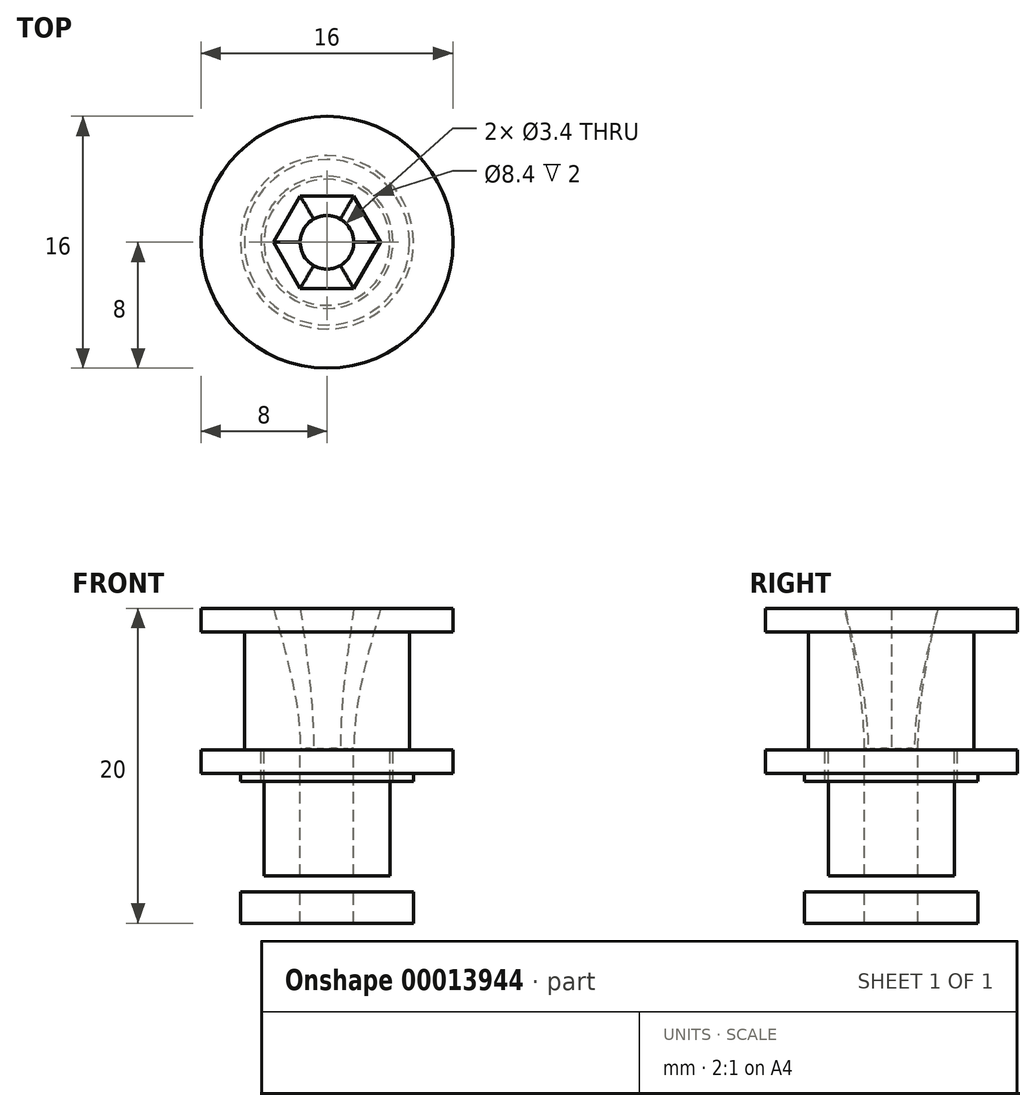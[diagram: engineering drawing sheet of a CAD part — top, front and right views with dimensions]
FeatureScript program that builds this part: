
annotation { "Feature Type Name" : "Feature", "Feature Type Description" : "" }
export const myFeature = defineFeature(function(context is Context, id is Id, definition is map)
    precondition{}
    {
        {
            var Q0;
            Q0=qCreatedBy(makeId("Top.planeOp"),FACE);
            var sketch = newSketch(context, id + "F0", { "sketchPlane" : qUnion([Q0])});
            skLineSegment(sketch, "E0", {"start": v(-19.17, 17.78) * mm, "end": v(-18.17, 17.78) * mm});
            skLineSegment(sketch, "E1", {"start": v(-18.17, 17.78) * mm, "end": v(-18.17, 18.4) * mm});
            skArc(sketch, "E2", {"start": v(-18.67, 18.85) * mm, "mid": v(-18.88, 19.07) * mm, "end": v(-19.17, 19.16) * mm});
            skArc(sketch, "E3", {"start": v(-18.58, 18.54) * mm, "mid": v(-18.61, 18.7) * mm, "end": v(-18.67, 18.85) * mm});
            skArc(sketch, "E4", {"start": v(-18.58, 18.54) * mm, "mid": v(-18.53, 18.44) * mm, "end": v(-18.43, 18.4) * mm});
            skLineSegment(sketch, "E5", {"start": v(-18.43, 18.4) * mm, "end": v(-18.17, 18.4) * mm});
            skArc(sketch, "E6.0.MirrorCS", {"start": v(-19.67, 18.85) * mm, "mid": v(-19.47, 19.07) * mm, "end": v(-19.17, 19.16) * mm});
            skArc(sketch, "E7.0.MirrorCS", {"start": v(-19.76, 18.54) * mm, "mid": v(-19.73, 18.7) * mm, "end": v(-19.67, 18.85) * mm});
            skArc(sketch, "E8.0.MirrorCS", {"start": v(-19.76, 18.54) * mm, "mid": v(-19.81, 18.44) * mm, "end": v(-19.91, 18.4) * mm});
            skLineSegment(sketch, "E9.0.MirrorCS", {"start": v(-19.91, 18.4) * mm, "end": v(-20.17, 18.4) * mm});
            skLineSegment(sketch, "E10.0.MirrorCS", {"start": v(-20.17, 17.78) * mm, "end": v(-20.17, 18.4) * mm});
            skLineSegment(sketch, "E11.0.MirrorCS", {"start": v(-19.17, 17.78) * mm, "end": v(-20.17, 17.78) * mm});
            skLineSegment(sketch, "E12.direction1", {"start": v(-20.17, 17.78) * mm, "end": v(-18.17, 17.78) * mm, "construction": true});
            skLineSegment(sketch, "E13", {"start": v(-20.17, 18.15) * mm, "end": v(-18.17, 18.15) * mm, "construction": true});
            skPoint(sketch, "E14", {"position": v(0, -5.25) * mm});
            skArc(sketch, "E15", {"start": v(0.51, -5.6) * mm, "mid": v(0, -5.25) * mm, "end": v(-0.51, -5.6) * mm});
            skArc(sketch, "E16", {"start": v(-0.51, -5.6) * mm, "mid": v(-0.56, -5.71) * mm, "end": v(-0.59, -5.83) * mm});
            skArc(sketch, "E17", {"start": v(0.59, -5.83) * mm, "mid": v(0.56, -5.71) * mm, "end": v(0.51, -5.6) * mm});
            skArc(sketch, "E18", {"start": v(0.72, -5.96) * mm, "mid": v(0.94, -5.93) * mm, "end": v(1.16, -5.89) * mm});
            skArc(sketch, "E19", {"start": v(0.59, -5.83) * mm, "mid": v(0.66, -5.94) * mm, "end": v(0.8, -5.95) * mm});
            skArc(sketch, "E20", {"start": v(-0.59, -5.83) * mm, "mid": v(-0.66, -5.94) * mm, "end": v(-0.8, -5.95) * mm});
            skArc(sketch, "E21.1.0", {"start": v(2.22, -5.16) * mm, "mid": v(1.62, -5) * mm, "end": v(1.24, -5.48) * mm});
            skPoint(sketch, "E21.1.1", {"position": v(1.62, -5) * mm});
            skArc(sketch, "E21.1.2", {"start": v(1.24, -5.48) * mm, "mid": v(1.23, -5.6) * mm, "end": v(1.24, -5.73) * mm});
            skArc(sketch, "E21.1.3", {"start": v(2.36, -5.37) * mm, "mid": v(2.47, -5.44) * mm, "end": v(2.6, -5.41) * mm});
            skArc(sketch, "E21.1.4", {"start": v(1.24, -5.73) * mm, "mid": v(1.2, -5.85) * mm, "end": v(1.08, -5.9) * mm});
            skArc(sketch, "E21.1.5", {"start": v(2.36, -5.37) * mm, "mid": v(2.3, -5.26) * mm, "end": v(2.22, -5.16) * mm});
            skArc(sketch, "E22.3.2.0", {"start": v(3.7, -4.22) * mm, "mid": v(3.09, -4.25) * mm, "end": v(2.87, -4.83) * mm});
            skPoint(sketch, "E22.4.2.0", {"position": v(3.09, -4.25) * mm});
            skArc(sketch, "E22.5.2.0", {"start": v(2.87, -4.83) * mm, "mid": v(2.9, -4.95) * mm, "end": v(2.95, -5.07) * mm});
            skArc(sketch, "E22.9.2.0", {"start": v(3.9, -4.37) * mm, "mid": v(4.03, -4.41) * mm, "end": v(4.14, -4.35) * mm});
            skArc(sketch, "E22.13.2.0", {"start": v(2.95, -5.07) * mm, "mid": v(2.95, -5.2) * mm, "end": v(2.85, -5.28) * mm});
            skArc(sketch, "E22.17.2.0", {"start": v(3.9, -4.37) * mm, "mid": v(3.81, -4.3) * mm, "end": v(3.7, -4.22) * mm});
            skArc(sketch, "E22.3.3.0", {"start": v(4.83, -2.87) * mm, "mid": v(4.25, -3.09) * mm, "end": v(4.22, -3.7) * mm});
            skPoint(sketch, "E22.4.3.0", {"position": v(4.25, -3.09) * mm});
            skArc(sketch, "E22.5.3.0", {"start": v(4.22, -3.7) * mm, "mid": v(4.3, -3.81) * mm, "end": v(4.37, -3.9) * mm});
            skArc(sketch, "E22.9.3.0", {"start": v(5.07, -2.95) * mm, "mid": v(5.2, -2.95) * mm, "end": v(5.28, -2.85) * mm});
            skArc(sketch, "E22.13.3.0", {"start": v(4.37, -3.9) * mm, "mid": v(4.41, -4.03) * mm, "end": v(4.35, -4.14) * mm});
            skArc(sketch, "E22.17.3.0", {"start": v(5.07, -2.95) * mm, "mid": v(4.95, -2.9) * mm, "end": v(4.83, -2.87) * mm});
            skArc(sketch, "E22.3.4.0", {"start": v(5.48, -1.24) * mm, "mid": v(5, -1.62) * mm, "end": v(5.16, -2.22) * mm});
            skPoint(sketch, "E22.4.4.0", {"position": v(5, -1.62) * mm});
            skArc(sketch, "E22.5.4.0", {"start": v(5.16, -2.22) * mm, "mid": v(5.26, -2.3) * mm, "end": v(5.37, -2.36) * mm});
            skArc(sketch, "E22.9.4.0", {"start": v(5.73, -1.24) * mm, "mid": v(5.85, -1.2) * mm, "end": v(5.9, -1.08) * mm});
            skArc(sketch, "E22.13.4.0", {"start": v(5.37, -2.36) * mm, "mid": v(5.44, -2.47) * mm, "end": v(5.41, -2.6) * mm});
            skArc(sketch, "E22.17.4.0", {"start": v(5.73, -1.24) * mm, "mid": v(5.6, -1.23) * mm, "end": v(5.48, -1.24) * mm});
            skArc(sketch, "E22.3.5.0", {"start": v(5.6, 0.51) * mm, "mid": v(5.25, 0) * mm, "end": v(5.6, -0.51) * mm});
            skPoint(sketch, "E22.4.5.0", {"position": v(5.25, 0) * mm});
            skArc(sketch, "E22.5.5.0", {"start": v(5.6, -0.51) * mm, "mid": v(5.71, -0.56) * mm, "end": v(5.83, -0.59) * mm});
            skArc(sketch, "E22.9.5.0", {"start": v(5.83, 0.59) * mm, "mid": v(5.94, 0.66) * mm, "end": v(5.95, 0.8) * mm});
            skArc(sketch, "E22.13.5.0", {"start": v(5.83, -0.59) * mm, "mid": v(5.94, -0.66) * mm, "end": v(5.95, -0.8) * mm});
            skArc(sketch, "E22.17.5.0", {"start": v(5.83, 0.59) * mm, "mid": v(5.71, 0.56) * mm, "end": v(5.6, 0.51) * mm});
            skArc(sketch, "E22.3.6.0", {"start": v(5.16, 2.22) * mm, "mid": v(5, 1.62) * mm, "end": v(5.48, 1.24) * mm});
            skPoint(sketch, "E22.4.6.0", {"position": v(5, 1.62) * mm});
            skArc(sketch, "E22.5.6.0", {"start": v(5.48, 1.24) * mm, "mid": v(5.6, 1.23) * mm, "end": v(5.73, 1.24) * mm});
            skArc(sketch, "E22.9.6.0", {"start": v(5.37, 2.36) * mm, "mid": v(5.44, 2.47) * mm, "end": v(5.41, 2.6) * mm});
            skArc(sketch, "E22.13.6.0", {"start": v(5.73, 1.24) * mm, "mid": v(5.85, 1.2) * mm, "end": v(5.9, 1.08) * mm});
            skArc(sketch, "E22.17.6.0", {"start": v(5.37, 2.36) * mm, "mid": v(5.26, 2.3) * mm, "end": v(5.16, 2.22) * mm});
            skArc(sketch, "E22.3.7.0", {"start": v(4.22, 3.7) * mm, "mid": v(4.25, 3.09) * mm, "end": v(4.83, 2.87) * mm});
            skPoint(sketch, "E22.4.7.0", {"position": v(4.25, 3.09) * mm});
            skArc(sketch, "E22.5.7.0", {"start": v(4.83, 2.87) * mm, "mid": v(4.95, 2.9) * mm, "end": v(5.07, 2.95) * mm});
            skArc(sketch, "E22.9.7.0", {"start": v(4.37, 3.9) * mm, "mid": v(4.41, 4.03) * mm, "end": v(4.35, 4.14) * mm});
            skArc(sketch, "E22.13.7.0", {"start": v(5.07, 2.95) * mm, "mid": v(5.2, 2.95) * mm, "end": v(5.28, 2.85) * mm});
            skArc(sketch, "E22.17.7.0", {"start": v(4.37, 3.9) * mm, "mid": v(4.3, 3.81) * mm, "end": v(4.22, 3.7) * mm});
            skArc(sketch, "E22.3.8.0", {"start": v(2.87, 4.83) * mm, "mid": v(3.09, 4.25) * mm, "end": v(3.7, 4.22) * mm});
            skPoint(sketch, "E22.4.8.0", {"position": v(3.09, 4.25) * mm});
            skArc(sketch, "E22.5.8.0", {"start": v(3.7, 4.22) * mm, "mid": v(3.81, 4.3) * mm, "end": v(3.9, 4.37) * mm});
            skArc(sketch, "E22.9.8.0", {"start": v(2.95, 5.07) * mm, "mid": v(2.95, 5.2) * mm, "end": v(2.85, 5.28) * mm});
            skArc(sketch, "E22.13.8.0", {"start": v(3.9, 4.37) * mm, "mid": v(4.03, 4.41) * mm, "end": v(4.14, 4.35) * mm});
            skArc(sketch, "E22.17.8.0", {"start": v(2.95, 5.07) * mm, "mid": v(2.9, 4.95) * mm, "end": v(2.87, 4.83) * mm});
            skArc(sketch, "E22.3.9.0", {"start": v(1.24, 5.48) * mm, "mid": v(1.62, 5) * mm, "end": v(2.22, 5.16) * mm});
            skPoint(sketch, "E22.4.9.0", {"position": v(1.62, 5) * mm});
            skArc(sketch, "E22.5.9.0", {"start": v(2.22, 5.16) * mm, "mid": v(2.3, 5.26) * mm, "end": v(2.36, 5.37) * mm});
            skArc(sketch, "E22.9.9.0", {"start": v(1.24, 5.73) * mm, "mid": v(1.2, 5.85) * mm, "end": v(1.08, 5.9) * mm});
            skArc(sketch, "E22.13.9.0", {"start": v(2.36, 5.37) * mm, "mid": v(2.47, 5.44) * mm, "end": v(2.6, 5.41) * mm});
            skArc(sketch, "E22.17.9.0", {"start": v(1.24, 5.73) * mm, "mid": v(1.23, 5.6) * mm, "end": v(1.24, 5.48) * mm});
            skArc(sketch, "E22.3.10.0", {"start": v(-0.51, 5.6) * mm, "mid": v(0, 5.25) * mm, "end": v(0.51, 5.6) * mm});
            skPoint(sketch, "E22.4.10.0", {"position": v(0, 5.25) * mm});
            skArc(sketch, "E22.5.10.0", {"start": v(0.51, 5.6) * mm, "mid": v(0.56, 5.71) * mm, "end": v(0.59, 5.83) * mm});
            skArc(sketch, "E22.9.10.0", {"start": v(-0.59, 5.83) * mm, "mid": v(-0.66, 5.94) * mm, "end": v(-0.8, 5.95) * mm});
            skArc(sketch, "E22.13.10.0", {"start": v(0.59, 5.83) * mm, "mid": v(0.66, 5.94) * mm, "end": v(0.8, 5.95) * mm});
            skArc(sketch, "E22.17.10.0", {"start": v(-0.59, 5.83) * mm, "mid": v(-0.56, 5.71) * mm, "end": v(-0.51, 5.6) * mm});
            skArc(sketch, "E22.3.11.0", {"start": v(-2.22, 5.16) * mm, "mid": v(-1.62, 5) * mm, "end": v(-1.24, 5.48) * mm});
            skPoint(sketch, "E22.4.11.0", {"position": v(-1.62, 5) * mm});
            skArc(sketch, "E22.5.11.0", {"start": v(-1.24, 5.48) * mm, "mid": v(-1.23, 5.6) * mm, "end": v(-1.24, 5.73) * mm});
            skArc(sketch, "E22.9.11.0", {"start": v(-2.36, 5.37) * mm, "mid": v(-2.47, 5.44) * mm, "end": v(-2.6, 5.41) * mm});
            skArc(sketch, "E22.13.11.0", {"start": v(-1.24, 5.73) * mm, "mid": v(-1.2, 5.85) * mm, "end": v(-1.08, 5.9) * mm});
            skArc(sketch, "E22.17.11.0", {"start": v(-2.36, 5.37) * mm, "mid": v(-2.3, 5.26) * mm, "end": v(-2.22, 5.16) * mm});
            skArc(sketch, "E22.3.12.0", {"start": v(-3.7, 4.22) * mm, "mid": v(-3.09, 4.25) * mm, "end": v(-2.87, 4.83) * mm});
            skPoint(sketch, "E22.4.12.0", {"position": v(-3.09, 4.25) * mm});
            skArc(sketch, "E22.5.12.0", {"start": v(-2.87, 4.83) * mm, "mid": v(-2.9, 4.95) * mm, "end": v(-2.95, 5.07) * mm});
            skArc(sketch, "E22.9.12.0", {"start": v(-3.9, 4.37) * mm, "mid": v(-4.03, 4.41) * mm, "end": v(-4.14, 4.35) * mm});
            skArc(sketch, "E22.13.12.0", {"start": v(-2.95, 5.07) * mm, "mid": v(-2.95, 5.2) * mm, "end": v(-2.85, 5.28) * mm});
            skArc(sketch, "E22.17.12.0", {"start": v(-3.9, 4.37) * mm, "mid": v(-3.81, 4.3) * mm, "end": v(-3.7, 4.22) * mm});
            skArc(sketch, "E22.3.13.0", {"start": v(-4.83, 2.87) * mm, "mid": v(-4.25, 3.09) * mm, "end": v(-4.22, 3.7) * mm});
            skPoint(sketch, "E22.4.13.0", {"position": v(-4.25, 3.09) * mm});
            skArc(sketch, "E22.5.13.0", {"start": v(-4.22, 3.7) * mm, "mid": v(-4.3, 3.81) * mm, "end": v(-4.37, 3.9) * mm});
            skArc(sketch, "E22.9.13.0", {"start": v(-5.07, 2.95) * mm, "mid": v(-5.2, 2.95) * mm, "end": v(-5.28, 2.85) * mm});
            skArc(sketch, "E22.13.13.0", {"start": v(-4.37, 3.9) * mm, "mid": v(-4.41, 4.03) * mm, "end": v(-4.35, 4.14) * mm});
            skArc(sketch, "E22.17.13.0", {"start": v(-5.07, 2.95) * mm, "mid": v(-4.95, 2.9) * mm, "end": v(-4.83, 2.87) * mm});
            skArc(sketch, "E22.3.14.0", {"start": v(-5.48, 1.24) * mm, "mid": v(-5, 1.62) * mm, "end": v(-5.16, 2.22) * mm});
            skPoint(sketch, "E22.4.14.0", {"position": v(-5, 1.62) * mm});
            skArc(sketch, "E22.5.14.0", {"start": v(-5.16, 2.22) * mm, "mid": v(-5.26, 2.3) * mm, "end": v(-5.37, 2.36) * mm});
            skArc(sketch, "E22.9.14.0", {"start": v(-5.73, 1.24) * mm, "mid": v(-5.85, 1.2) * mm, "end": v(-5.9, 1.08) * mm});
            skArc(sketch, "E22.13.14.0", {"start": v(-5.37, 2.36) * mm, "mid": v(-5.44, 2.47) * mm, "end": v(-5.41, 2.6) * mm});
            skArc(sketch, "E22.17.14.0", {"start": v(-5.73, 1.24) * mm, "mid": v(-5.6, 1.23) * mm, "end": v(-5.48, 1.24) * mm});
            skArc(sketch, "E22.3.15.0", {"start": v(-5.6, -0.51) * mm, "mid": v(-5.25, 0) * mm, "end": v(-5.6, 0.51) * mm});
            skPoint(sketch, "E22.4.15.0", {"position": v(-5.25, 0) * mm});
            skArc(sketch, "E22.5.15.0", {"start": v(-5.6, 0.51) * mm, "mid": v(-5.71, 0.56) * mm, "end": v(-5.83, 0.59) * mm});
            skArc(sketch, "E22.9.15.0", {"start": v(-5.83, -0.59) * mm, "mid": v(-5.94, -0.66) * mm, "end": v(-5.95, -0.8) * mm});
            skArc(sketch, "E22.13.15.0", {"start": v(-5.83, 0.59) * mm, "mid": v(-5.94, 0.66) * mm, "end": v(-5.95, 0.8) * mm});
            skArc(sketch, "E22.17.15.0", {"start": v(-5.83, -0.59) * mm, "mid": v(-5.71, -0.56) * mm, "end": v(-5.6, -0.51) * mm});
            skArc(sketch, "E22.3.16.0", {"start": v(-5.16, -2.22) * mm, "mid": v(-5, -1.62) * mm, "end": v(-5.48, -1.24) * mm});
            skPoint(sketch, "E22.4.16.0", {"position": v(-5, -1.62) * mm});
            skArc(sketch, "E22.5.16.0", {"start": v(-5.48, -1.24) * mm, "mid": v(-5.6, -1.23) * mm, "end": v(-5.73, -1.24) * mm});
            skArc(sketch, "E22.9.16.0", {"start": v(-5.37, -2.36) * mm, "mid": v(-5.44, -2.47) * mm, "end": v(-5.41, -2.6) * mm});
            skArc(sketch, "E22.13.16.0", {"start": v(-5.73, -1.24) * mm, "mid": v(-5.85, -1.2) * mm, "end": v(-5.9, -1.08) * mm});
            skArc(sketch, "E22.17.16.0", {"start": v(-5.37, -2.36) * mm, "mid": v(-5.26, -2.3) * mm, "end": v(-5.16, -2.22) * mm});
            skArc(sketch, "E22.3.17.0", {"start": v(-4.22, -3.7) * mm, "mid": v(-4.25, -3.09) * mm, "end": v(-4.83, -2.87) * mm});
            skPoint(sketch, "E22.4.17.0", {"position": v(-4.25, -3.09) * mm});
            skArc(sketch, "E22.5.17.0", {"start": v(-4.83, -2.87) * mm, "mid": v(-4.95, -2.9) * mm, "end": v(-5.07, -2.95) * mm});
            skArc(sketch, "E22.9.17.0", {"start": v(-4.37, -3.9) * mm, "mid": v(-4.41, -4.03) * mm, "end": v(-4.35, -4.14) * mm});
            skArc(sketch, "E22.13.17.0", {"start": v(-5.07, -2.95) * mm, "mid": v(-5.2, -2.95) * mm, "end": v(-5.28, -2.85) * mm});
            skArc(sketch, "E22.17.17.0", {"start": v(-4.37, -3.9) * mm, "mid": v(-4.3, -3.81) * mm, "end": v(-4.22, -3.7) * mm});
            skArc(sketch, "E22.3.18.0", {"start": v(-2.87, -4.83) * mm, "mid": v(-3.09, -4.25) * mm, "end": v(-3.7, -4.22) * mm});
            skPoint(sketch, "E22.4.18.0", {"position": v(-3.09, -4.25) * mm});
            skArc(sketch, "E22.5.18.0", {"start": v(-3.7, -4.22) * mm, "mid": v(-3.81, -4.3) * mm, "end": v(-3.9, -4.37) * mm});
            skArc(sketch, "E22.9.18.0", {"start": v(-2.95, -5.07) * mm, "mid": v(-2.95, -5.2) * mm, "end": v(-2.85, -5.28) * mm});
            skArc(sketch, "E22.13.18.0", {"start": v(-3.9, -4.37) * mm, "mid": v(-4.03, -4.41) * mm, "end": v(-4.14, -4.35) * mm});
            skArc(sketch, "E22.17.18.0", {"start": v(-2.95, -5.07) * mm, "mid": v(-2.9, -4.95) * mm, "end": v(-2.87, -4.83) * mm});
            skArc(sketch, "E22.3.19.0", {"start": v(-1.24, -5.48) * mm, "mid": v(-1.62, -5) * mm, "end": v(-2.22, -5.16) * mm});
            skPoint(sketch, "E22.4.19.0", {"position": v(-1.62, -5) * mm});
            skArc(sketch, "E22.5.19.0", {"start": v(-2.22, -5.16) * mm, "mid": v(-2.3, -5.26) * mm, "end": v(-2.36, -5.37) * mm});
            skArc(sketch, "E22.9.19.0", {"start": v(-1.24, -5.73) * mm, "mid": v(-1.2, -5.85) * mm, "end": v(-1.08, -5.9) * mm});
            skArc(sketch, "E22.13.19.0", {"start": v(-2.36, -5.37) * mm, "mid": v(-2.47, -5.44) * mm, "end": v(-2.6, -5.41) * mm});
            skArc(sketch, "E22.17.19.0", {"start": v(-1.24, -5.73) * mm, "mid": v(-1.23, -5.6) * mm, "end": v(-1.24, -5.48) * mm});
            skArc(sketch, "E23.trimOffspring", {"start": v(2.52, -5.44) * mm, "mid": v(2.72, -5.35) * mm, "end": v(2.92, -5.24) * mm});
            skArc(sketch, "E24.trimOffspring", {"start": v(4.08, -4.4) * mm, "mid": v(4.24, -4.24) * mm, "end": v(4.4, -4.08) * mm});
            skArc(sketch, "E25.trimOffspring", {"start": v(5.24, -2.92) * mm, "mid": v(5.33, -2.76) * mm, "end": v(5.41, -2.6) * mm});
            skArc(sketch, "E26.trimOffspring", {"start": v(5.89, -1.16) * mm, "mid": v(5.93, -0.94) * mm, "end": v(5.96, -0.72) * mm});
            skArc(sketch, "E27.trimOffspring", {"start": v(5.44, 2.52) * mm, "mid": v(5.35, 2.72) * mm, "end": v(5.24, 2.92) * mm});
            skArc(sketch, "E28.trimOffspring", {"start": v(4.4, 4.08) * mm, "mid": v(4.24, 4.24) * mm, "end": v(4.08, 4.4) * mm});
            skArc(sketch, "E29.trimOffspring", {"start": v(5.96, 0.72) * mm, "mid": v(5.93, 0.94) * mm, "end": v(5.89, 1.16) * mm});
            skArc(sketch, "E30.trimOffspring", {"start": v(2.92, 5.24) * mm, "mid": v(2.72, 5.35) * mm, "end": v(2.52, 5.44) * mm});
            skArc(sketch, "E31.trimOffspring", {"start": v(1.16, 5.89) * mm, "mid": v(0.94, 5.93) * mm, "end": v(0.72, 5.96) * mm});
            skArc(sketch, "E32.trimOffspring", {"start": v(-0.72, 5.96) * mm, "mid": v(-0.94, 5.93) * mm, "end": v(-1.16, 5.89) * mm});
            skArc(sketch, "E33.trimOffspring", {"start": v(-2.52, 5.44) * mm, "mid": v(-2.72, 5.35) * mm, "end": v(-2.92, 5.24) * mm});
            skArc(sketch, "E34.trimOffspring", {"start": v(-4.08, 4.4) * mm, "mid": v(-4.24, 4.24) * mm, "end": v(-4.4, 4.08) * mm});
            skArc(sketch, "E35.trimOffspring", {"start": v(-5.24, 2.92) * mm, "mid": v(-5.35, 2.72) * mm, "end": v(-5.44, 2.52) * mm});
            skArc(sketch, "E36.trimOffspring", {"start": v(-5.89, 1.16) * mm, "mid": v(-5.93, 0.94) * mm, "end": v(-5.96, 0.72) * mm});
            skArc(sketch, "E37.trimOffspring", {"start": v(-5.96, -0.72) * mm, "mid": v(-5.93, -0.94) * mm, "end": v(-5.89, -1.16) * mm});
            skArc(sketch, "E38.trimOffspring", {"start": v(-5.44, -2.52) * mm, "mid": v(-5.35, -2.72) * mm, "end": v(-5.24, -2.92) * mm});
            skArc(sketch, "E39.trimOffspring", {"start": v(-4.4, -4.08) * mm, "mid": v(-4.24, -4.24) * mm, "end": v(-4.08, -4.4) * mm});
            skArc(sketch, "E40.trimOffspring", {"start": v(-2.92, -5.24) * mm, "mid": v(-2.72, -5.35) * mm, "end": v(-2.52, -5.44) * mm});
            skArc(sketch, "E41.trimOffspring", {"start": v(-1.16, -5.89) * mm, "mid": v(-0.94, -5.93) * mm, "end": v(-0.72, -5.96) * mm});
            skCircle(sketch, "E42", {"center": v(0, 0) * mm, "radius": 5.25 * mm});
            skSolve(sketch);
        }
        {
            var Q0;
            {var subQ0=sQuery(id+"F0.wireOp",EDGE,"E42");var subQ1=makeQuery(id+"F0.imprint","INTERSECT",VERTEX,{"derivedFrom":[sQuery(id+"F0.wireOp",EDGE,"E22.3.5.0"),subQ0]});Q0=makeQuery(id+"F0.imprint","IMPRINT",FACE,{"disambiguationData":[TD([[makeQuery(id+"F0.imprint","IMPRINT",EDGE,{"disambiguationData":[TD([[subQ1,-1.0]])],"derivedFrom":subQ0}),1.0]])]});}
            extrude(context, id + "F1", {"entities" : qUnion([Q0]), "depth" : 7.5 * mm});
        }
        {
            var Q0;
            Q0=makeQuery(id+"F1.opExtrude","CAP_FACE",FACE,{"disambiguationData":[OSD([sQuery(id+"F0.wireOp",EDGE,"E42")])],"isStart":false});
            var sketch = newSketch(context, id + "F2", { "sketchPlane" : qUnion([Q0])});
            skCircle(sketch, "E43", {"center": v(0, 0) * mm, "radius": 8 * mm});
            skSolve(sketch);
        }
        {
            var Q0;
            Q0=qSketchRegion(id+"F2",true);
            extrude(context, id + "F3", {"entities" : qUnion([Q0]), "operationType" : NewBodyOperationType.ADD, "depth" : 1.5 * mm});
        }
        {
            var Q0;
            Q0=makeQuery(id+"F1.opExtrude","CAP_FACE",FACE,{"disambiguationData":[OSD([sQuery(id+"F0.wireOp",EDGE,"E42")])],"isStart":true});
            var sketch = newSketch(context, id + "F4", { "sketchPlane" : qUnion([Q0])});
            skCircle(sketch, "E44.0", {"center": v(0, 0) * mm, "radius": 8 * mm});
            skCircle(sketch, "E45", {"center": v(0, 0) * mm, "radius": 4.2 * mm});
            skSolve(sketch);
        }
        {
            var Q0;
            Q0=qSketchRegion(id+"F4",true);
            extrude(context, id + "F5", {"entities" : qUnion([Q0]), "depth" : 1.5 * mm});
        }
        {
            var Q0;
            Q0=makeQuery(id+"F5.opExtrude","CAP_FACE",FACE,{"disambiguationData":[OSD([sQuery(id+"F4.wireOp",EDGE,"E44.0")])],"isStart":false});
            var sketch = newSketch(context, id + "F6", { "sketchPlane" : qUnion([Q0])});
            skCircle(sketch, "E46", {"center": v(0, 0) * mm, "radius": 5.5 * mm});
            skCircle(sketch, "E47", {"center": v(0, 0) * mm, "radius": 4.2 * mm});
            skSolve(sketch);
        }
        {
            var Q0;
            Q0=makeQuery(id+"F6.imprint","IMPRINT",FACE,{"disambiguationData":[TD([[makeQuery(id+"F6.imprint","IMPRINT",EDGE,{"derivedFrom":sQuery(id+"F6.wireOp",EDGE,"E46")}),1.0]])]});
            extrude(context, id + "F7", {"entities" : qUnion([Q0]), "operationType" : NewBodyOperationType.ADD, "depth" : 0.5 * mm});
        }
        {
            var Q0;
            Q0=makeQuery(id+"F1.opExtrude","CAP_FACE",FACE,{"disambiguationData":[OSD([sQuery(id+"F0.wireOp",EDGE,"E42")])],"isStart":true});
            var sketch = newSketch(context, id + "F8", { "sketchPlane" : qUnion([Q0])});
            skCircle(sketch, "E48", {"center": v(0, 0) * mm, "radius": 4 * mm});
            skSolve(sketch);
        }
        {
            var Q0;
            Q0=qSketchRegion(id+"F8",true);
            extrude(context, id + "F9", {"entities" : qUnion([Q0]), "operationType" : NewBodyOperationType.ADD, "depth" : 8 * mm});
        }
        {
            var Q0;
            Q0=qCreatedBy(makeId("Top.planeOp"),FACE);
            var sketch = newSketch(context, id + "F10", { "sketchPlane" : qUnion([Q0])});
            skCircle(sketch, "E49", {"center": v(0, 0) * mm, "radius": 1.7 * mm});
            skSolve(sketch);
        }
        {
            var Q0;
            Q0=makeQuery(id+"F3.opExtrude","CAP_FACE",FACE,{"disambiguationData":[OSD([sQuery(id+"F2.wireOp",EDGE,"E43")])],"isStart":false});
            var sketch = newSketch(context, id + "F11", { "sketchPlane" : qUnion([Q0])});
            skCircle(sketch, "E50.cCircle", {"center": v(0, 0) * mm, "radius": 2.95 * mm, "construction": true});
            skLineSegment(sketch, "E50.0", {"start": v(3.4, 0) * mm, "end": v(1.7, -2.95) * mm});
            skLineSegment(sketch, "E50.1", {"start": v(1.7, -2.95) * mm, "end": v(-1.7, -2.95) * mm});
            skLineSegment(sketch, "E50.2", {"start": v(-1.7, -2.95) * mm, "end": v(-3.4, 0) * mm});
            skLineSegment(sketch, "E50.3", {"start": v(-3.4, 0) * mm, "end": v(-1.7, 2.95) * mm});
            skLineSegment(sketch, "E50.4", {"start": v(-1.7, 2.95) * mm, "end": v(1.7, 2.95) * mm});
            skLineSegment(sketch, "E50.5", {"start": v(1.7, 2.95) * mm, "end": v(3.4, 0) * mm});
            skPoint(sketch, "E50.0.midPoint", {"position": v(2.55, -1.48) * mm});
            skSolve(sketch);
        }
        {
            var Q0;
            Q0=qSketchRegion(id+"F10",true);
            extrude(context, id + "F12", {"entities" : qUnion([Q0]), "operationType" : NewBodyOperationType.REMOVE, "endBound" : BoundingType.SYMMETRIC, "oppositeDirection" : true, "depth" : 25 * mm});
        }
        {
            var Q1;
            Q1 = qSketchRegion(id + "F11", true);
            var Q2;
            Q2 = qSketchRegion(id + "F10", true);
            var Q3;
            Q3 = qConstructionFilter(qBodyType(qCreatedBy(id + "F11" ,EDGE), BodyType.WIRE), ConstructionObject.NO);
            var Q4;
            Q4 = qConstructionFilter(qBodyType(qCreatedBy(id + "F10" ,EDGE), BodyType.WIRE), ConstructionObject.NO);
            loft(context, id + "F13", {"operationType" : NewBodyOperationType.REMOVE, "endCondition" : LoftEndDerivativeType.NORMAL_TO_PROFILE, "endMagnitude" : 1, "sheetProfilesArray" : [{ "sheetProfileEntities" : qUnion([Q1]) }, { "sheetProfileEntities" : qUnion([Q2]) }], "wireProfilesArray" : [{ "wireProfileEntities" : qUnion([Q3]) }, { "wireProfileEntities" : qUnion([Q4]) }]});
        }
        {
            var Q0;
            Q0=qCreatedBy(makeId("Top.planeOp"),FACE);
            cPlane(context, id + "F14", {"entities" : qUnion([Q0]), "cplaneType" : CPlaneType.OFFSET, "offset" : 9 * mm, "oppositeDirection" : true, "width" : 150 * mm, "height" : 150 * mm});
        }
        {
            var Q0;
            Q0=qCreatedBy(id+"F14.planeOp",FACE);
            var sketch = newSketch(context, id + "F15", { "sketchPlane" : qUnion([Q0])});
            skCircle(sketch, "E51.0", {"center": v(0, 0) * mm, "radius": 1.7 * mm});
            skCircle(sketch, "E52.0", {"center": v(0, 0) * mm, "radius": 5.5 * mm});
            skSolve(sketch);
        }
        {
            var Q0;
            Q0=qSketchRegion(id+"F15",true);
            extrude(context, id + "F16", {"entities" : qUnion([Q0]), "oppositeDirection" : true, "depth" : 2 * mm});
        }
    });
